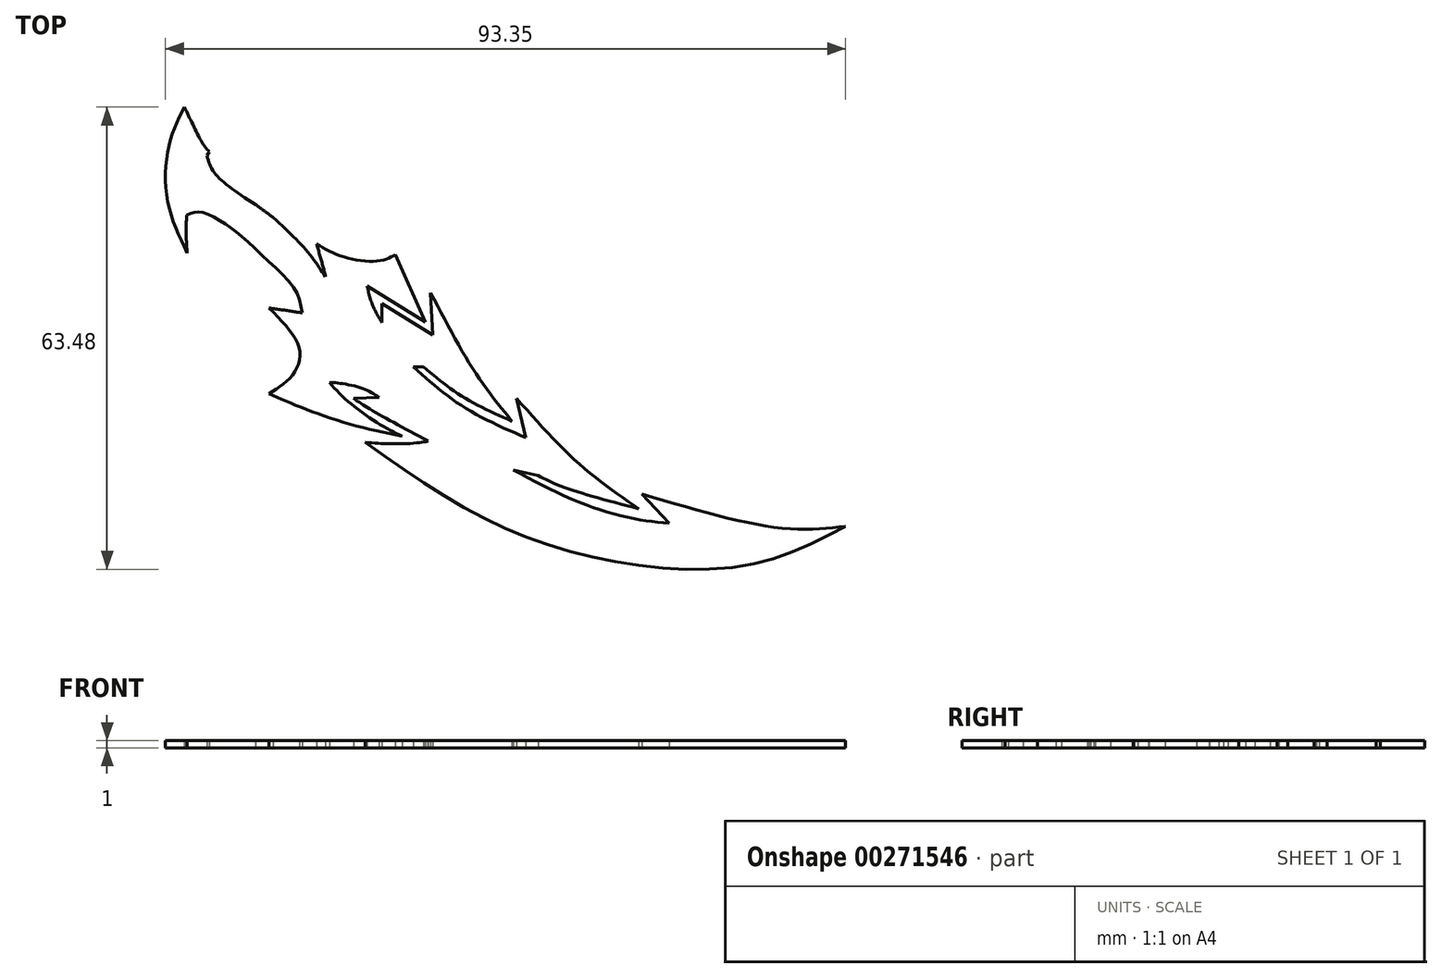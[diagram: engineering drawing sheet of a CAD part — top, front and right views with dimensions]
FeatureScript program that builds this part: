
annotation { "Feature Type Name" : "Feature", "Feature Type Description" : "" }
export const myFeature = defineFeature(function(context is Context, id is Id, definition is map)
    precondition{}
    {
        {
            var Q0;
            Q0=qCreatedBy(makeId("Top.planeOp"),FACE);
            var sketch = newSketch(context, id + "F0", { "sketchPlane" : qUnion([Q0])});
            skFitSpline(sketch, "E0", {"points": [v(-16.6, 10.22) * mm, v(-12.72, 8.4) * mm, v(-7.78, 7.95) * mm, v(-5.79, 8.78) * mm], "startDerivative": vector(9.92, -5.75) * mm, "endDerivative": vector(6.63, 3.98) * mm});
            skLineSegment(sketch, "E1", {"start": v(-5.79, 8.78) * mm, "end": v(-1.65, -0.5) * mm});
            skLineSegment(sketch, "E2", {"start": v(-1.65, -0.5) * mm, "end": v(-9.65, 4.48) * mm});
            skFitSpline(sketch, "E3", {"points": [v(-9.65, 4.48) * mm, v(-8.96, 1.94) * mm, v(-7.67, -0.55) * mm], "startDerivative": vector(1.12, -5.23) * mm, "endDerivative": vector(2.85, -4.82) * mm});
            skLineSegment(sketch, "E4", {"start": v(-7.67, -0.55) * mm, "end": v(-7.67, 2.05) * mm});
            skLineSegment(sketch, "E5", {"start": v(-7.67, 2.05) * mm, "end": v(-0.69, -2.28) * mm});
            skLineSegment(sketch, "E6", {"start": v(-0.69, -2.28) * mm, "end": v(-0.94, 3.52) * mm});
            skFitSpline(sketch, "E7", {"points": [v(-0.94, 3.52) * mm, v(5.07, -7.26) * mm, v(10.22, -14.12) * mm], "startDerivative": vector(10.95, -21.05) * mm, "endDerivative": vector(11.4, -14.01) * mm});
            skFitSpline(sketch, "E8", {"points": [v(10.22, -14.12) * mm, v(3.33, -10.67) * mm, v(-1.9, -6.62) * mm], "startDerivative": vector(-13.9, 6.18) * mm, "endDerivative": vector(-10.31, 8.84) * mm});
            skLineSegment(sketch, "E9", {"start": v(-1.9, -6.62) * mm, "end": v(-3.31, -6.62) * mm});
            skFitSpline(sketch, "E10", {"points": [v(-3.31, -6.62) * mm, v(3.33, -11.99) * mm, v(12.1, -16.37) * mm], "startDerivative": vector(12.99, -11.75) * mm, "endDerivative": vector(17.77, -7.78) * mm});
            skLineSegment(sketch, "E11", {"start": v(12.1, -16.37) * mm, "end": v(10.85, -10.99) * mm});
            skFitSpline(sketch, "E12", {"points": [v(10.85, -10.99) * mm, v(19.57, -20.08) * mm, v(27.62, -26.12) * mm], "startDerivative": vector(16.38, -18.39) * mm, "endDerivative": vector(17.19, -11.76) * mm});
            skFitSpline(sketch, "E13", {"points": [v(27.62, -26.12) * mm, v(17.1, -23.1) * mm, v(13.83, -21.57) * mm], "startDerivative": vector(-18.97, 4.94) * mm, "endDerivative": vector(-7.6, 4.1) * mm});
            skLineSegment(sketch, "E14", {"start": v(13.83, -21.57) * mm, "end": v(10.42, -20.8) * mm});
            skFitSpline(sketch, "E15", {"points": [v(10.42, -20.8) * mm, v(19.08, -25.1) * mm, v(26.59, -27.41) * mm, v(31.78, -28.13) * mm], "startDerivative": vector(22.83, -12.28) * mm, "endDerivative": vector(17.83, -1.82) * mm});
            skLineSegment(sketch, "E16", {"start": v(31.78, -28.13) * mm, "end": v(28.02, -24.1) * mm});
            skFitSpline(sketch, "E17", {"points": [v(28.02, -24.1) * mm, v(46.94, -28.75) * mm, v(56.01, -28.55) * mm], "startDerivative": vector(34.64, -10.28) * mm, "endDerivative": vector(20.45, 2.16) * mm});
            skFitSpline(sketch, "E18", {"points": [v(56.01, -28.55) * mm, v(42.96, -33.77) * mm, v(24.21, -33.37) * mm, v(6.52, -27.5) * mm, v(-9.92, -17.02) * mm], "startDerivative": vector(-54.78, -28.5) * mm, "endDerivative": vector(-61.45, 43.42) * mm});
            skFitSpline(sketch, "E19", {"points": [v(-9.92, -17.02) * mm, v(-4.21, -17.18) * mm, v(-1.3, -16.82) * mm, v(-1.3, -16.8) * mm], "startDerivative": vector(10.09, -0.69) * mm, "endDerivative": vector(-0.33, 0.7) * mm});
            skFitSpline(sketch, "E20", {"points": [v(-1.3, -16.8) * mm, v(-9.17, -12.51) * mm, v(-11.53, -10.98) * mm], "startDerivative": vector(-14.12, 7.47) * mm, "endDerivative": vector(-5.54, 3.84) * mm});
            skLineSegment(sketch, "E21", {"start": v(-11.53, -10.98) * mm, "end": v(-8.02, -10.82) * mm});
            skFitSpline(sketch, "E22", {"points": [v(-8.02, -10.82) * mm, v(-10.5, -9.54) * mm, v(-14.1, -8.82) * mm, v(-14.85, -8.83) * mm], "startDerivative": vector(-5.76, 3.69) * mm, "endDerivative": vector(-2.98, -0.28) * mm});
            skFitSpline(sketch, "E23", {"points": [v(-14.85, -8.83) * mm, v(-12.1, -11.54) * mm, v(-7.83, -14.6) * mm, v(-4.85, -16.16) * mm], "startDerivative": vector(7.72, -8.24) * mm, "endDerivative": vector(9.37, -4.47) * mm});
            skFitSpline(sketch, "E24", {"points": [v(-4.85, -16.16) * mm, v(-12.54, -14.36) * mm, v(-19.39, -11.94) * mm, v(-23.12, -10.34) * mm], "startDerivative": vector(-20.58, 4.22) * mm, "endDerivative": vector(-12.83, 5.68) * mm});
            skFitSpline(sketch, "E25", {"points": [v(-23.12, -10.34) * mm, v(-19.89, -7.72) * mm, v(-19, -4.06) * mm, v(-23.12, 1.42) * mm], "startDerivative": vector(11.7, 7.46) * mm, "endDerivative": vector(-13.93, 13.93) * mm});
            skFitSpline(sketch, "E26", {"points": [v(-23.12, 1.42) * mm, v(-20.54, 1.07) * mm, v(-18.6, 0.76) * mm], "startDerivative": vector(5, -0.67) * mm, "endDerivative": vector(4.03, -0.65) * mm});
            skFitSpline(sketch, "E27", {"points": [v(-16.6, 10.22) * mm, v(-15.92, 7.88) * mm, v(-15.37, 5.7) * mm], "startDerivative": vector(1.4, -4.62) * mm, "endDerivative": vector(1.08, -4.4) * mm});
            skFitSpline(sketch, "E28", {"points": [v(-34.76, 29.03) * mm, v(-36.86, 23.78) * mm, v(-37.02, 16) * mm, v(-34.36, 9) * mm], "startDerivative": vector(-8.07, -16.2) * mm, "endDerivative": vector(9.48, -19.38) * mm});
            skFitSpline(sketch, "E29", {"points": [v(-34.76, 29.03) * mm, v(-33.48, 26.4) * mm, v(-32.17, 23.91) * mm, v(-31.35, 22.9) * mm], "startDerivative": vector(3.32, -6.8) * mm, "endDerivative": vector(3.18, -3.45) * mm});
            skFitSpline(sketch, "E30", {"points": [v(-34.36, 9) * mm, v(-34.5, 12.11) * mm, v(-34.36, 15.21) * mm], "startDerivative": vector(-0.52, 6.22) * mm, "endDerivative": vector(0.52, 6.21) * mm});
            skFitSpline(sketch, "E31", {"points": [v(-31.65, 22.35) * mm, v(-31, 20.52) * mm, v(-29.17, 18.57) * mm, v(-24.5, 15.37) * mm, v(-19.04, 12.78) * mm, v(-18.12, 12.6) * mm], "startDerivative": vector(3.11, -11.94) * mm, "endDerivative": vector(6.6, -0.53) * mm});
            skLineSegment(sketch, "E32", {"start": v(-18.56, 0.9) * mm, "end": v(-18.6, 0.76) * mm});
            skLineSegment(sketch, "E33", {"start": v(-18.12, 12.6) * mm, "end": v(-15.37, 5.7) * mm});
            skLineSegment(sketch, "E34", {"start": v(-31.35, 22.9) * mm, "end": v(-31.65, 22.35) * mm});
            skFitSpline(sketch, "E35", {"points": [v(-23.72, 14.94) * mm, v(-18.2, 9.55) * mm, v(-15.37, 5.7) * mm], "startDerivative": vector(10.82, -9.91) * mm, "endDerivative": vector(5.67, -8.53) * mm});
            skFitSpline(sketch, "E36", {"points": [v(-18.6, 0.76) * mm, v(-19.46, 3.74) * mm, v(-22.86, 7.52) * mm, v(-27.08, 11.44) * mm, v(-29.59, 13.24) * mm, v(-32.11, 14.52) * mm, v(-33.34, 14.58) * mm, v(-34.45, 14.18) * mm], "startDerivative": vector(-3.27, 20.5) * mm, "endDerivative": vector(-12.25, -5.4) * mm});
            skFitSpline(sketch, "E37", {"points": [v(-24.98, 15.65) * mm, v(-23.6, 14.63) * mm, v(-22.54, 13.86) * mm], "startDerivative": vector(2.66, -2.01) * mm, "endDerivative": vector(2.18, -1.62) * mm});
            skSolve(sketch);
        }
        {
            var Q0;
            Q0=makeQuery(id+"F0.imprint","IMPRINT",FACE,{"disambiguationData":[TD([[makeQuery(id+"F0.imprint","IMPRINT",EDGE,{"derivedFrom":sQuery(id+"F0.wireOp",EDGE,"E0")}),-1.0]])]});
            var Q1;
            {var subQ0=sQuery(id+"F0.wireOp",EDGE,"038a0a4f-5dde-4097-ba5c-28771c0dbc60");Q1=makeQuery(id+"F0.imprint","IMPRINT",FACE,{"disambiguationData":[TD([[makeQuery(id+"F0.imprint","IMPRINT",EDGE,{"derivedFrom":subQ0}),-1.0]])]});}
            extrude(context, id + "F1", {"entities" : qUnion([Q0, Q1]), "depth" : 1 * mm, "offsetDistance" : 25 * mm});
        }
    });
